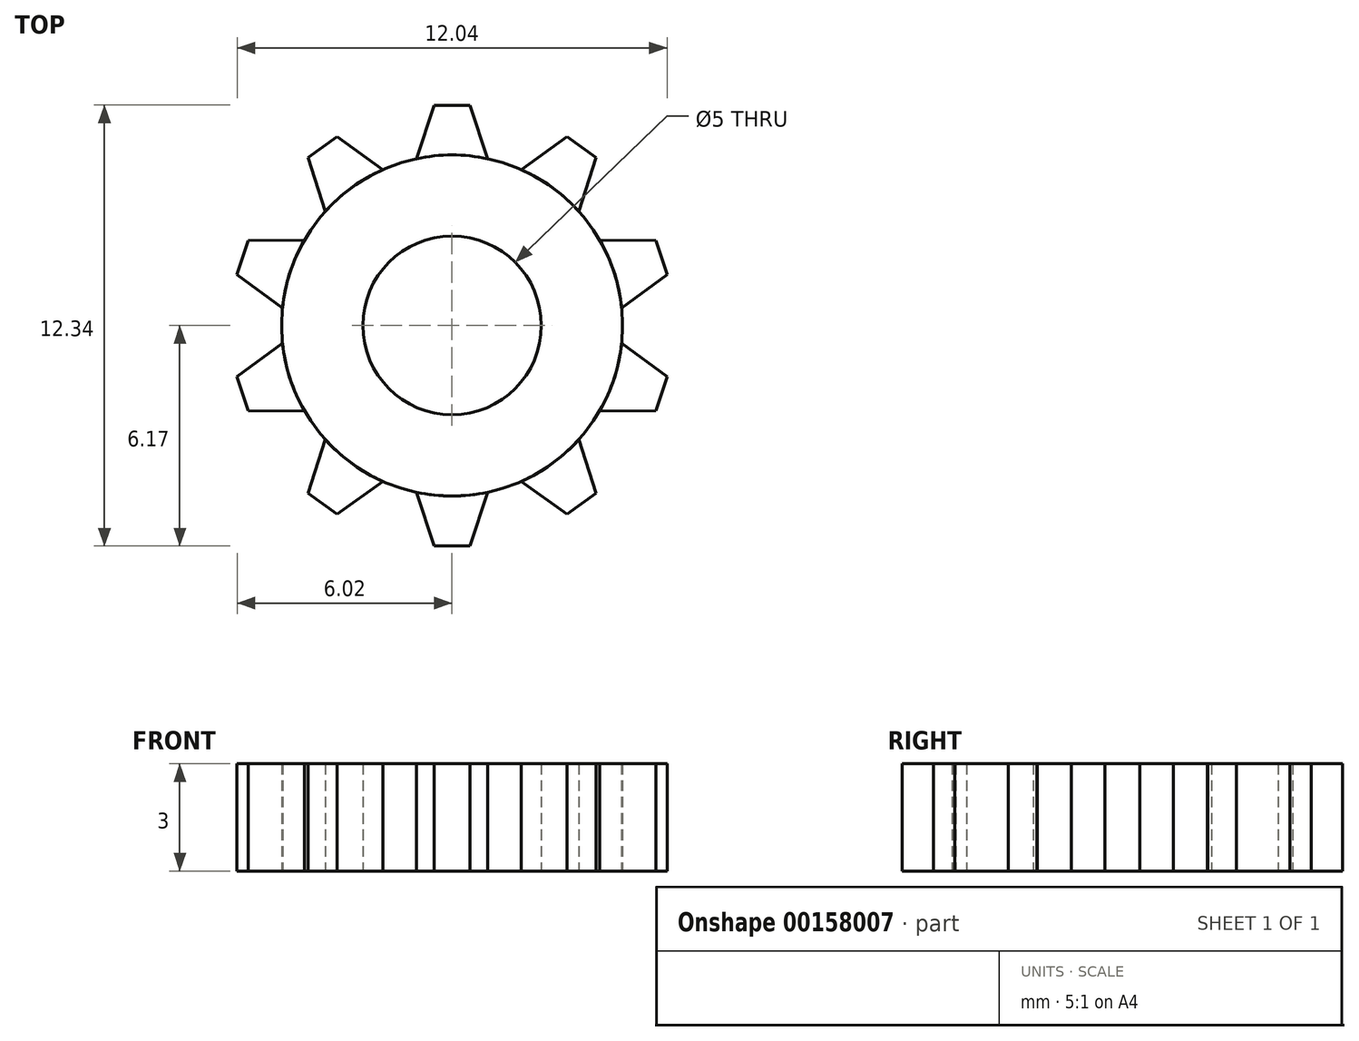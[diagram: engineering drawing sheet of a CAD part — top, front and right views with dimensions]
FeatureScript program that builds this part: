
annotation { "Feature Type Name" : "Feature", "Feature Type Description" : "" }
export const myFeature = defineFeature(function(context is Context, id is Id, definition is map)
    precondition{}
    {
        {
            var Q0;
            Q0=qCreatedBy(makeId("Top.planeOp"),FACE);
            var sketch = newSketch(context, id + "F0", { "sketchPlane" : qUnion([Q0])});
            skCircle(sketch, "E0", {"center": v(0, 0) * mm, "radius": 4.77 * mm});
            skCircle(sketch, "E1", {"center": v(0, 0) * mm, "radius": 2.5 * mm});
            skSolve(sketch);
        }
        {
            var Q0;
            Q0=makeQuery(id+"F0.imprint","IMPRINT",FACE,{"disambiguationData":[TD([[makeQuery(id+"F0.imprint","IMPRINT",EDGE,{"derivedFrom":sQuery(id+"F0.wireOp",EDGE,"E0")}),1.0]])]});
            var sketch = newSketch(context, id + "F1", { "sketchPlane" : qUnion([Q0])});
            skCircle(sketch, "E2.0", {"center": v(0, 0) * mm, "radius": 4.77 * mm});
            skLineSegment(sketch, "E3", {"start": v(-1, 4.67) * mm, "end": v(-0.5, 6.17) * mm});
            skLineSegment(sketch, "E4", {"start": v(-0.5, 6.17) * mm, "end": v(0.5, 6.17) * mm});
            skLineSegment(sketch, "E5", {"start": v(0.5, 6.17) * mm, "end": v(1, 4.67) * mm});
            skSolve(sketch);
        }
        {
            var Q0;
            Q0=makeQuery(id+"F0.imprint","IMPRINT",FACE,{"disambiguationData":[TD([[makeQuery(id+"F0.imprint","IMPRINT",EDGE,{"derivedFrom":sQuery(id+"F0.wireOp",EDGE,"E0")}),1.0]])]});
            var Q1;
            {var subQ0=sQuery(id+"F1.wireOp",EDGE,"E3");Q1=makeQuery(id+"F1.imprint","IMPRINT",FACE,{"disambiguationData":[TD([[makeQuery(id+"F1.imprint","IMPRINT",EDGE,{"derivedFrom":subQ0}),-1.0]])]});}
            extrude(context, id + "F2", {"entities" : qUnion([Q0, Q1]), "depth" : 3 * mm});
        }
        {
            var Q0;
            Q0=makeQuery(id+"F2.opExtrude","SWEPT_BODY",BODY,{"disambiguationData":[OSD([sQuery(id+"F1.wireOp",EDGE,"E2.0"),sQuery(id+"F1.wireOp",EDGE,"E3"),sQuery(id+"F1.wireOp",EDGE,"E4"),sQuery(id+"F1.wireOp",EDGE,"E5")])]});
            var Q1;
            Q1=makeQuery(id+"F2.opExtrude","CAP_EDGE",EDGE,{"disambiguationData":[OSD([sQuery(id+"F0.wireOp",EDGE,"E0")])],"isStart":false});
            circularPattern(context, id + "F3", {"entities" : qUnion([Q0]), "axis" : qUnion([Q1]), "angle" : 36 * degree, "instanceCount" : 10});
        }
    });
